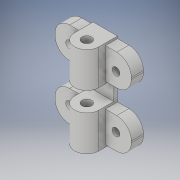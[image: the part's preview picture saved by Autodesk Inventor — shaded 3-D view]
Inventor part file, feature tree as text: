
AUTODESK INVENTOR PART (.ipt)
format: ipt  version: 2018 (Build 220112000, 112)  size: 202,240 bytes
history: native  units: in
note: dims shown in document units (in); Inventor stores cm internally (conversion verified against a paired STEP export)
features: extrude x6, sketch x4, fillet x2, plane x1
ambient origin geometry x8: Origin, YZ Plane, XZ Plane, XY Plane, X Axis, Y Axis, Z Axis, Center Point
bodies: Solid1 (feature_tree)
feature tree (13):
  sketch  "Sketch1"  dims[d0=0.3937in d1=1.46in]
  extrude  "Extrusion1"  Depth=1.46in
  extrude  "Extrusion2"  Depth=0.5in
  extrude  "Extrusion3"  Depth=0.5in
  fillet  "Fillet1"  Radius=0.4965in
  fillet  "Fillet2"  Radius=0.1969in
  extrude  "Extrusion4"  Depth=0.1969in
  extrude  "Extrusion5"  Depth=0.2362in
  plane  "Work Plane1"
  extrude  "Extrusion6"  Depth=0.315in
  sketch  "Sketch2"  dims[d2=0.42in d3=0.5in]
  sketch  "Sketch3"  dims[d4=0.42in d5=0.5in d6=0.4965in d7=0.0in d8=0.1969in d9=0.0in]
  sketch  "Sketch4"  dims[d10=0.1969in d11=0.0in d12=0.1969in d13=0.2362in d14=0.125in d15=0.85in d16=0.75in d17=0.125in d18=0.125in d19=0.125in d20=0.1969in d21=0.0in d22=0.1575in d23=3.937in d24=0.0in d25=0.4386in d26=0.315in d27=0.0in]
